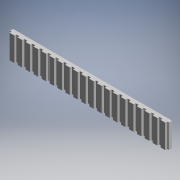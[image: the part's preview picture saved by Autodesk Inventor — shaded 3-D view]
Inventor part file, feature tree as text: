
AUTODESK INVENTOR PART (.ipt)
format: ipt  version: 2017.3 (Build 213256000, 256)  size: 262,144 bytes
history: native  units: mm (DEFAULTED — no unit token found)
features: extrude x1, sketch x1
ambient origin geometry x8: Origin, YZ Plane, XZ Plane, XY Plane, X Axis, Y Axis, Z Axis, Center Point
bodies: Solid1 (feature_tree)
feature tree (2):
  extrude  "Extrusion1"  [1 undecoded]
  sketch  "Sketch_1"  dims[d0=15.0mm d1=0.0mm]
note: 1 required parameter value undecoded (feature->parameter linkage not recoverable at this tier; creation-order binding heuristic only, values carry confidence <= 0.55)
